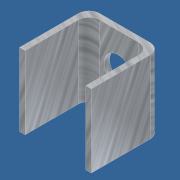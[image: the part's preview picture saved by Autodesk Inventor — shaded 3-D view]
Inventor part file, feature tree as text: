
AUTODESK INVENTOR PART (.ipt)
format: ipt  version: 2012 (Build 160160000, 160)  size: 134,144 bytes
history: native  units: in
note: dims shown in document units (in); Inventor stores cm internally (conversion verified against a paired STEP export)
features: sketch x4, extrude x2, fillet x2, hole x1
ambient origin geometry x8: Origin, YZ Plane, XZ Plane, XY Plane, X Axis, Y Axis, Z Axis, Center Point
bodies: Solid1 (feature_tree)
feature tree (9):
  extrude  "Extrusion1"  Depth=0.34in
  extrude  "Extrusion2"  Depth=0.026in
  fillet  "Fillet1"  Radius=0.026in
  fillet  "Fillet2"  Radius=0.298in
  hole  "Hole1"  [1 undecoded]
  sketch  "Sketch4"  dims[d10=0.131in d11=0.5in d12=0.375in d13=0.25in d14=0.5635in d15=0.75in d16=0.8108in]
  sketch  "Sketch1"  dims[d0=0.335in d1=0.34in]
  sketch  "Sketch2"  dims[d2=0.026in d3=0.0in d4=0.026in d5=0.026in d6=0.298in d7=0.0in]
  sketch  "Sketch3"  dims[d8=0.05in d9=0.05in]
note: 1 required parameter value undecoded (feature->parameter linkage not recoverable at this tier; creation-order binding heuristic only, values carry confidence <= 0.55)
